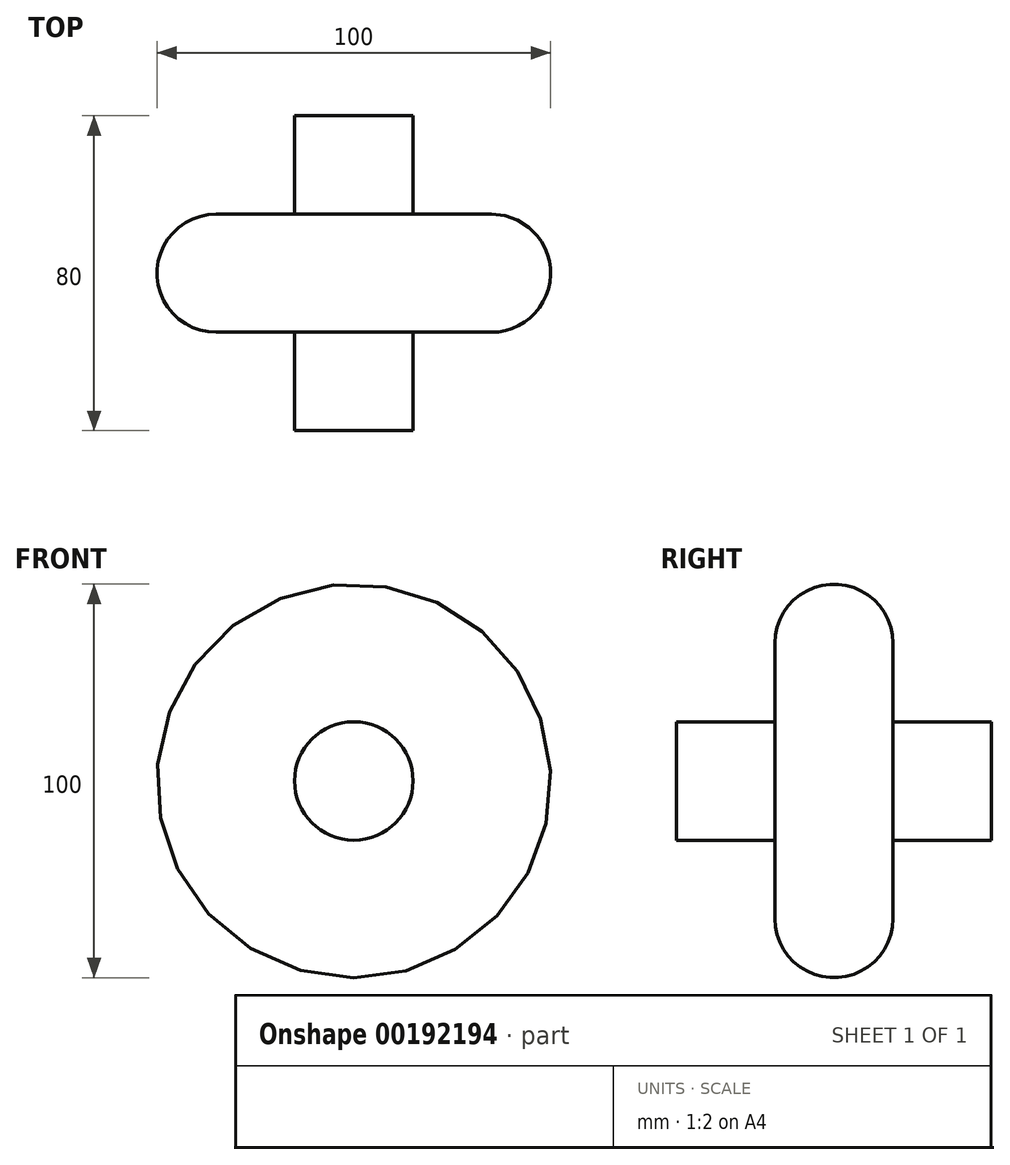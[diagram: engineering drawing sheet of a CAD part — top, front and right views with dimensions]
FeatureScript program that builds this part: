
annotation { "Feature Type Name" : "Feature", "Feature Type Description" : "" }
export const myFeature = defineFeature(function(context is Context, id is Id, definition is map)
    precondition{}
    {
        {
            var Q0;
            Q0=qCreatedBy(makeId("Front.planeOp"),FACE);
            var sketch = newSketch(context, id + "F0", { "sketchPlane" : qUnion([Q0])});
            skCircle(sketch, "E0", {"center": v(0, 0) * mm, "radius": 50 * mm});
            skCircle(sketch, "E1", {"center": v(0, 0) * mm, "radius": 15.05 * mm});
            skSolve(sketch);
        }
        {
            var Q0;
            Q0=makeQuery(id+"F0.imprint","IMPRINT",FACE,{"disambiguationData":[TD([[makeQuery(id+"F0.imprint","IMPRINT",EDGE,{"derivedFrom":sQuery(id+"F0.wireOp",EDGE,"E1")}),1.0]])]});
            extrude(context, id + "F1", {"entities" : qUnion([Q0]), "depth" : 80 * mm, "symmetric" : true});
        }
        {
            var Q0;
            Q0 = qSketchRegion(id + "F0", true);
            extrude(context, id + "F2", {"entities" : qUnion([Q0]), "operationType" : NewBodyOperationType.ADD, "depth" : 30 * mm, "symmetric" : true});
        }
        {
            var Q0;
            Q0=makeQuery(id+"F2.opExtrude","CAP_EDGE",EDGE,{"disambiguationData":[OSD([sQuery(id+"F0.wireOp",EDGE,"E0")])],"isStart":false});
            var Q1;
            Q1=makeQuery(id+"F2.opExtrude","CAP_EDGE",EDGE,{"disambiguationData":[OSD([sQuery(id+"F0.wireOp",EDGE,"E0")])],"isStart":true});
            fillet(context, id + "F3", {"entities" : qUnion([Q0, Q1]), "radius" : 15 * mm, "tangentPropagation" : true, "allowEdgeOverflow" : false});
        }
    });
